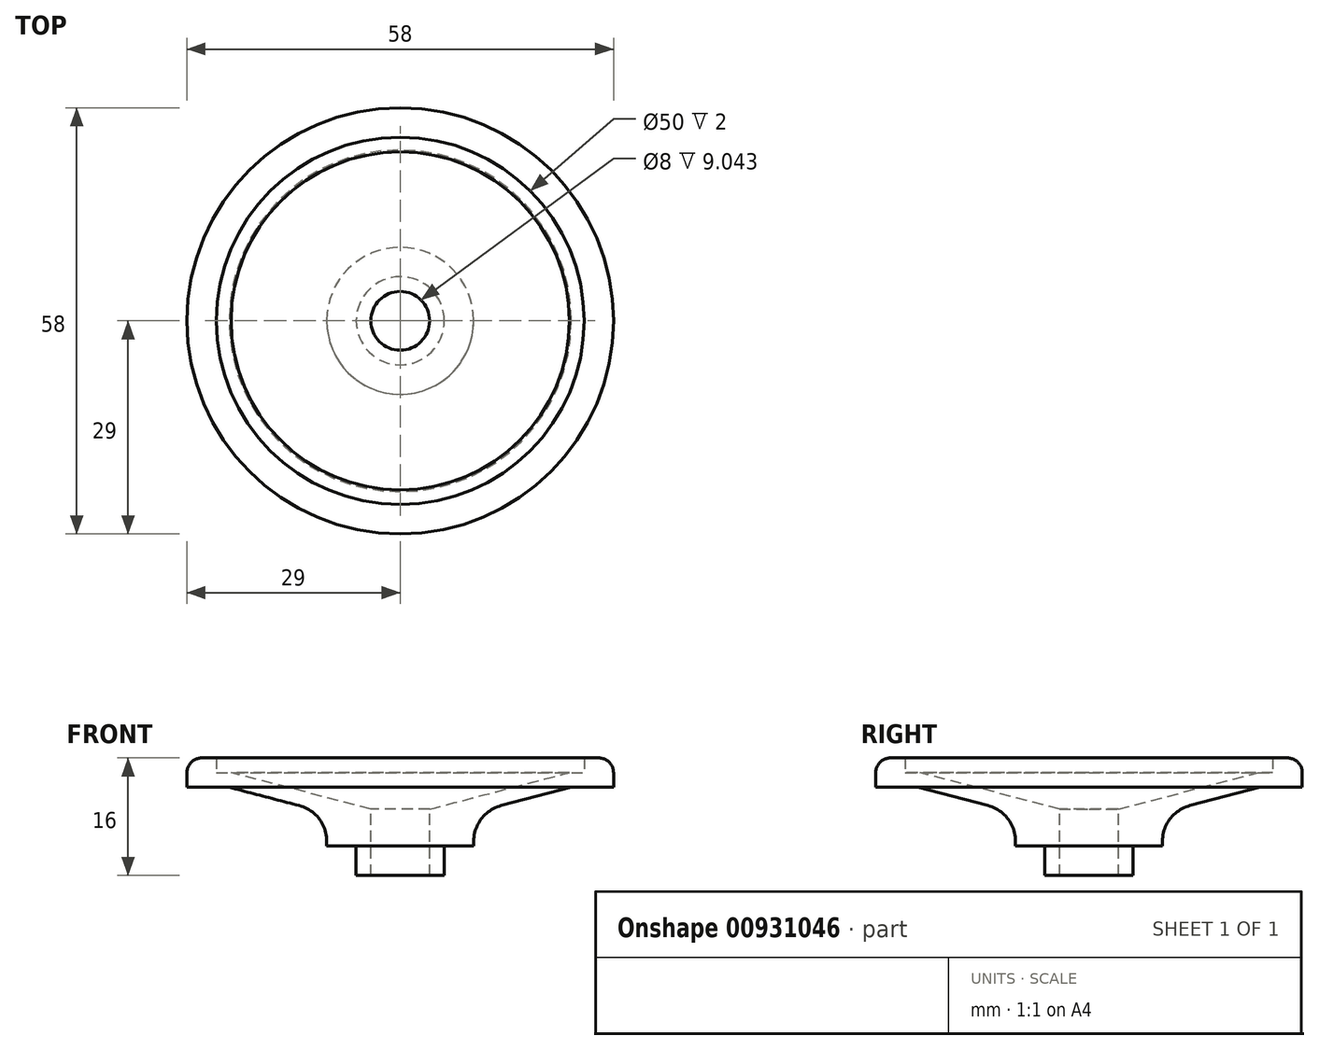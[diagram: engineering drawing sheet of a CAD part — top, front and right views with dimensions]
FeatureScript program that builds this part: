
annotation { "Feature Type Name" : "Feature", "Feature Type Description" : "" }
export const myFeature = defineFeature(function(context is Context, id is Id, definition is map)
    precondition{}
    {
        {
            var Q0;
            Q0=qCreatedBy(makeId("Right.planeOp"),FACE);
            var sketch = newSketch(context, id + "F0", { "sketchPlane" : qUnion([Q0])});
            skLineSegment(sketch, "E0.bottom", {"start": v(-25, 0) * mm, "end": v(-29, 0) * mm});
            skLineSegment(sketch, "E0.top", {"start": v(-25, 4) * mm, "end": v(-29, 4) * mm});
            skLineSegment(sketch, "E0.left", {"start": v(-25, 0) * mm, "end": v(-25, 4) * mm});
            skLineSegment(sketch, "E0.right", {"start": v(-29, 0) * mm, "end": v(-29, 4) * mm});
            skLineSegment(sketch, "E1.bottom", {"start": v(-25, 4) * mm, "end": v(-27, 4) * mm});
            skLineSegment(sketch, "E1.top", {"start": v(-25, 8) * mm, "end": v(-27, 8) * mm});
            skLineSegment(sketch, "E1.left", {"start": v(-25, 4) * mm, "end": v(-25, 8) * mm});
            skLineSegment(sketch, "E1.right", {"start": v(-27, 4) * mm, "end": v(-27, 8) * mm});
            skLineSegment(sketch, "E2.bottom", {"start": v(-25, 0) * mm, "end": v(-23.26, 0) * mm});
            skLineSegment(sketch, "E2.top", {"start": v(-25, 2) * mm, "end": v(-23, 2) * mm});
            skLineSegment(sketch, "E2.left", {"start": v(-25, 0) * mm, "end": v(-25, 2) * mm});
            skLineSegment(sketch, "E2.right", {"start": v(0, 0) * mm, "end": v(0, 2) * mm});
            skLineSegment(sketch, "E3", {"start": v(0, -4) * mm, "end": v(-23, 2) * mm});
            skLineSegment(sketch, "E4", {"start": v(-23.26, 0) * mm, "end": v(0, -6.07) * mm});
            skLineSegment(sketch, "E5", {"start": v(0, -6.07) * mm, "end": v(0, -4) * mm});
            skSolve(sketch);
        }
        {
            var Q0;
            Q0=makeQuery(id+"F0.imprint","IMPRINT",FACE,{"disambiguationData":[TD([[makeQuery(id+"F0.imprint","IMPRINT",EDGE,{"derivedFrom":sQuery(id+"F0.wireOp",EDGE,"E1.bottom")}),-1.0]])]});
            var Q1;
            Q1=makeQuery(id+"F0.imprint","IMPRINT",FACE,{"disambiguationData":[TD([[makeQuery(id+"F0.imprint","IMPRINT",EDGE,{"derivedFrom":sQuery(id+"F0.wireOp",EDGE,"E0.bottom")}),-1.0]])]});
            var Q2;
            Q2=makeQuery(id+"F0.imprint","IMPRINT",FACE,{"disambiguationData":[TD([[makeQuery(id+"F0.imprint","IMPRINT",EDGE,{"derivedFrom":sQuery(id+"F0.wireOp",EDGE,"E2.bottom")}),1.0]])]});
            var Q3;
            Q3=sQuery(id+"F0.wireOp",EDGE,"E2.right");
            revolve(context, id + "F1", {"surfaceOperationType" : NewSurfaceOperationType.NEW, "entities" : qUnion([Q0, Q1, Q2]), "axis" : qUnion([Q3]), "revolveType" : RevolveType.FULL});
        }
        {
            var Q0;
            Q0=qCreatedBy(makeId("Right.planeOp"),FACE);
            var sketch = newSketch(context, id + "F2", { "sketchPlane" : qUnion([Q0])});
            skLineSegment(sketch, "E6", {"start": v(0, -6.07) * mm, "end": v(-23.26, 0) * mm, "construction": true});
            skLineSegment(sketch, "E7", {"start": v(23, 2) * mm, "end": v(0, -4) * mm, "construction": true});
            skLineSegment(sketch, "E8", {"start": v(23.26, 0) * mm, "end": v(0, -6.07) * mm, "construction": true});
            skLineSegment(sketch, "E9.right", {"start": v(-6, -8) * mm, "end": v(-6, -12) * mm});
            skLineSegment(sketch, "E10.bottom", {"start": v(-6, -8) * mm, "end": v(-10, -8) * mm});
            skLineSegment(sketch, "E11", {"start": v(-10, -8) * mm, "end": v(-10, -1.4) * mm});
            skLineSegment(sketch, "E12", {"start": v(0, -4) * mm, "end": v(-23, 2) * mm, "construction": true});
            skLineSegment(sketch, "E13", {"start": v(-10, -1.4) * mm, "end": v(0, -4) * mm});
            skLineSegment(sketch, "E14", {"start": v(-6, -12) * mm, "end": v(0, -12) * mm});
            skLineSegment(sketch, "E15", {"start": v(0, -12) * mm, "end": v(0, -4) * mm});
            skSolve(sketch);
        }
        {
            var Q0;
            Q0=makeQuery(id+"F2.imprint","IMPRINT",FACE,{"disambiguationData":[TD([[makeQuery(id+"F2.imprint","IMPRINT",EDGE,{"derivedFrom":sQuery(id+"F2.wireOp",EDGE,"E9.bottom")}),1.0]])]});
            var Q1;
            Q1=makeQuery(id+"F2.imprint","IMPRINT",FACE,{"disambiguationData":[TD([[makeQuery(id+"F2.imprint","IMPRINT",EDGE,{"derivedFrom":sQuery(id+"F2.wireOp",EDGE,"E10.bottom")}),-1.0]])]});
            var Q2;
            Q2=sQuery(id+"F2.wireOp",EDGE,"E15");
            revolve(context, id + "F3", {"operationType" : NewBodyOperationType.ADD, "surfaceOperationType" : NewSurfaceOperationType.NEW, "entities" : qUnion([Q0, Q1]), "axis" : qUnion([Q2]), "revolveType" : RevolveType.FULL});
        }
        {
            var Q0;
            Q0=makeQuery(id+"F3.boolean.opBoolean","INTERSECT",EDGE,{"derivedFrom":[makeQuery(id+"F1.opRevolve","SWEPT_FACE",FACE,{"disambiguationData":[OSD([sQuery(id+"F0.wireOp",EDGE,"E4")])]}),makeQuery(id+"F3.opRevolve","SWEPT_FACE",FACE,{"disambiguationData":[OSD([sQuery(id+"F2.wireOp",EDGE,"E11")])]})]});
            fillet(context, id + "F4", {"entities" : qUnion([Q0]), "radius" : 5 * mm, "tangentPropagation" : true, "allowEdgeOverflow" : false});
        }
        {
            var Q0;
            Q0=qCreatedBy(makeId("Top.planeOp"),FACE);
            var sketch = newSketch(context, id + "F5", { "sketchPlane" : qUnion([Q0])});
            skCircle(sketch, "E16", {"center": v(0, 0) * mm, "radius": 4 * mm});
            skSolve(sketch);
        }
        {
            var Q0;
            Q0=makeQuery(id+"F5.imprint","IMPRINT",FACE,{"disambiguationData":[TD([[makeQuery(id+"F5.imprint","IMPRINT",EDGE,{"derivedFrom":sQuery(id+"F5.wireOp",EDGE,"E16")}),1.0]])]});
            extrude(context, id + "F6", {"entities" : qUnion([Q0]), "operationType" : NewBodyOperationType.REMOVE, "oppositeDirection" : true, "depth" : 25 * mm, "offsetDistance" : 25 * mm});
        }
        {
            var Q0;
            Q0=makeQuery(id+"F1.opRevolve","SWEPT_EDGE",EDGE,{"disambiguationData":[OSD([sQuery(id+"F0.wireOp",EDGE,"E0.top"),sQuery(id+"F0.wireOp",EDGE,"E1.bottom"),sQuery(id+"F0.wireOp",EDGE,"E1.right")])]});
            fillet(context, id + "F7", {"entities" : qUnion([Q0]), "radius" : 2 * mm, "tangentPropagation" : true, "allowEdgeOverflow" : false});
        }
    });
